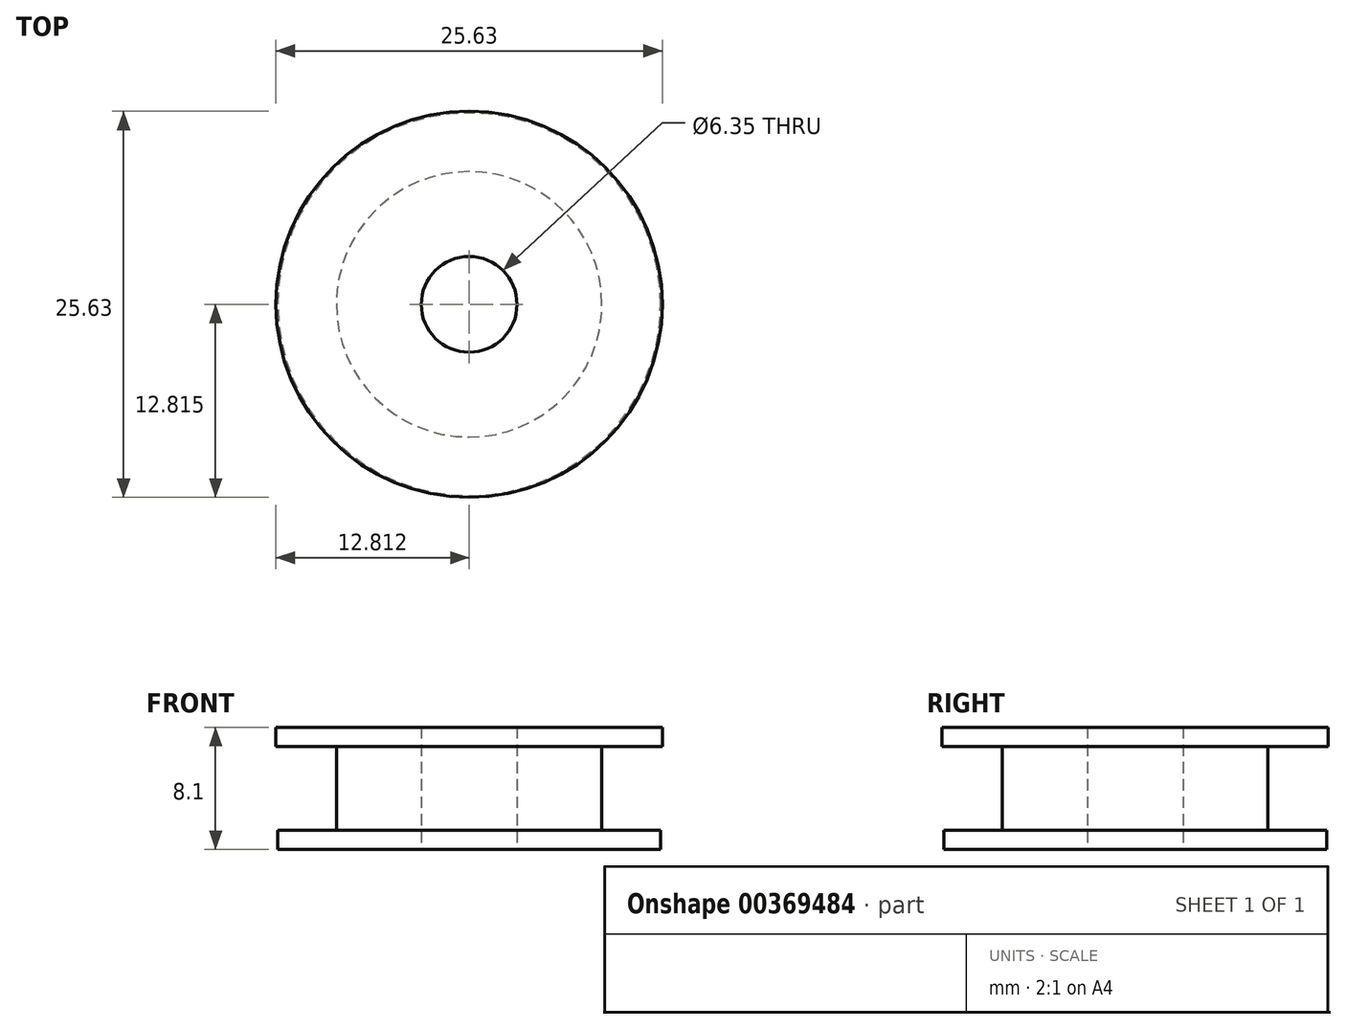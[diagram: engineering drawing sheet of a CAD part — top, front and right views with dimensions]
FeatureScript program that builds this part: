
annotation { "Feature Type Name" : "Feature", "Feature Type Description" : "" }
export const myFeature = defineFeature(function(context is Context, id is Id, definition is map)
    precondition{}
    {
        {
            var Q0;
            Q0=qCreatedBy(makeId("Top.planeOp"),FACE);
            var sketch = newSketch(context, id + "F0", { "sketchPlane" : qUnion([Q0])});
            skCircle(sketch, "E0", {"center": v(-24.46, 35.45) * mm, "radius": 12.7 * mm});
            skCircle(sketch, "E1", {"center": v(-24.46, 35.45) * mm, "radius": 3.18 * mm});
            skSolve(sketch);
        }
        {
            var Q0;
            Q0 = qSketchRegion(id + "F0", true);
            extrude(context, id + "F1", {"entities" : qUnion([Q0]), "depth" : 1.27 * mm});
        }
        {
            var Q0;
            Q0=makeQuery(id+"F1.opExtrude","CAP_FACE",FACE,{"disambiguationData":[OSD([sQuery(id+"F0.wireOp",EDGE,"E0"),sQuery(id+"F0.wireOp",EDGE,"E1")])],"isStart":false});
            var sketch = newSketch(context, id + "F2", { "sketchPlane" : qUnion([Q0])});
            skCircle(sketch, "E2", {"center": v(-24.46, 35.45) * mm, "radius": 8.8 * mm});
            skSolve(sketch);
        }
        {
            var Q0;
            Q0=makeQuery(id+"F2.imprint","IMPRINT",FACE,{"disambiguationData":[TD([[makeQuery(id+"F2.imprint","IMPRINT",EDGE,{"derivedFrom":sQuery(id+"F2.wireOp",EDGE,"E2")}),1.0]])]});
            extrude(context, id + "F3", {"entities" : qUnion([Q0]), "operationType" : NewBodyOperationType.ADD, "depth" : 5.56 * mm});
        }
        {
            var Q0;
            Q0=makeQuery(id+"F3.opExtrude","CAP_FACE",FACE,{"disambiguationData":[OSD([sQuery(id+"F0.wireOp",EDGE,"E1"),sQuery(id+"F2.wireOp",EDGE,"E2")])],"isStart":false});
            var sketch = newSketch(context, id + "F4", { "sketchPlane" : qUnion([Q0])});
            skCircle(sketch, "E3", {"center": v(-24.46, 35.45) * mm, "radius": 12.82 * mm});
            skSolve(sketch);
        }
        {
            var Q0;
            Q0=makeQuery(id+"F4.imprint","IMPRINT",FACE,{"disambiguationData":[TD([[makeQuery(id+"F4.imprint","IMPRINT",EDGE,{"derivedFrom":makeQuery(id+"F3.opExtrude","CAP_EDGE",EDGE,{"disambiguationData":[OSD([sQuery(id+"F2.wireOp",EDGE,"E2")])],"isStart":false})}),1.0]])]});
            var Q1;
            Q1=makeQuery(id+"F4.imprint","IMPRINT",FACE,{"disambiguationData":[TD([[makeQuery(id+"F4.imprint","IMPRINT",EDGE,{"derivedFrom":sQuery(id+"F4.wireOp",EDGE,"E3")}),1.0]])]});
            extrude(context, id + "F5", {"entities" : qUnion([Q0, Q1]), "operationType" : NewBodyOperationType.ADD, "depth" : 1.27 * mm});
        }
    });
